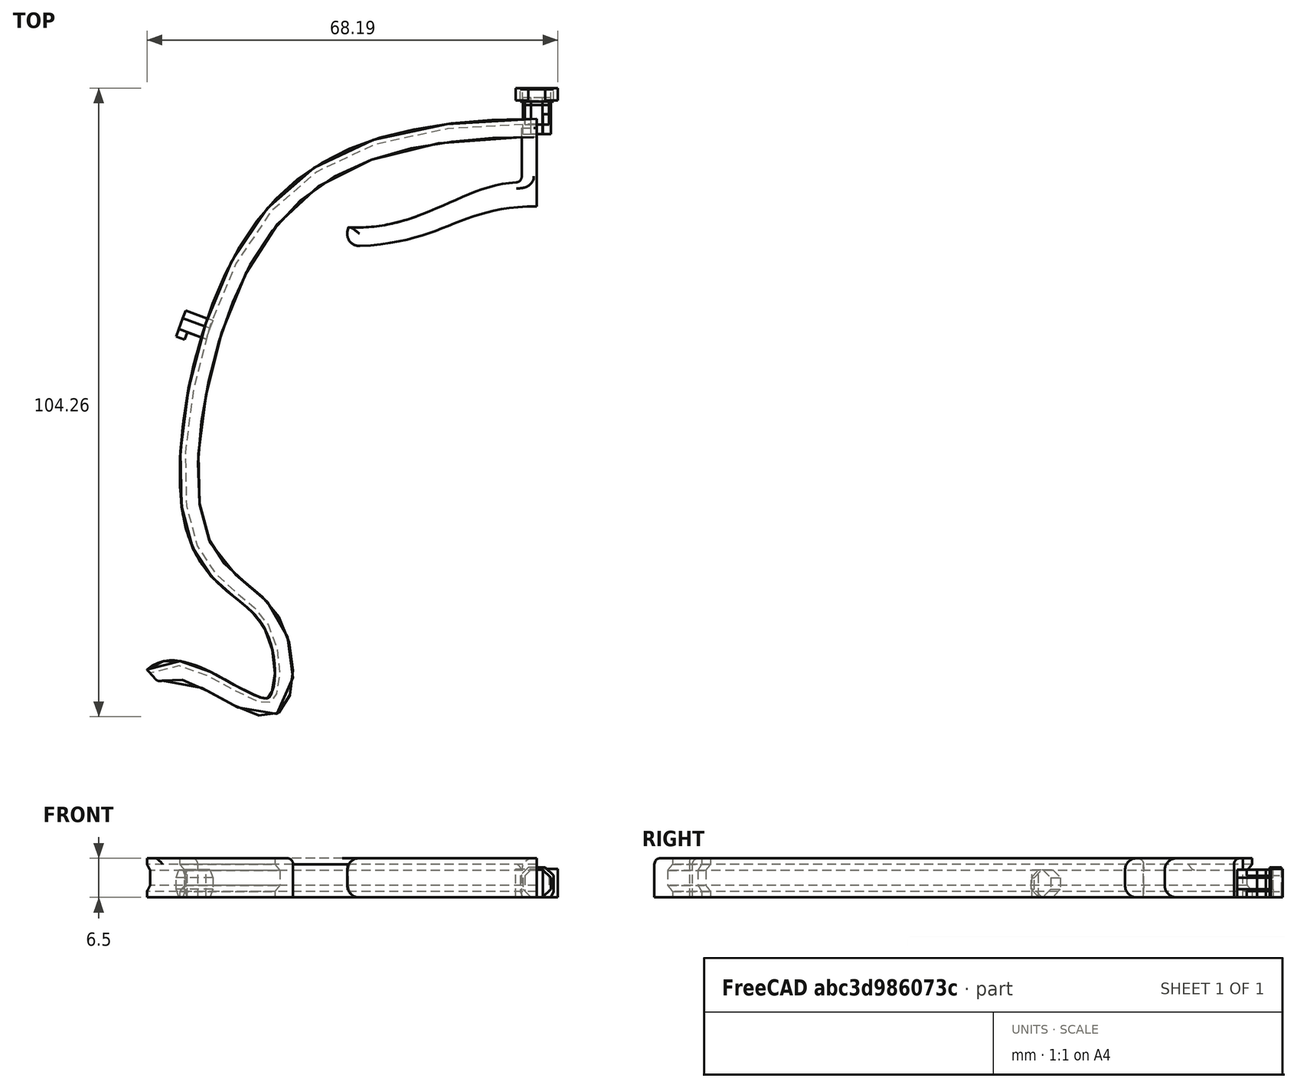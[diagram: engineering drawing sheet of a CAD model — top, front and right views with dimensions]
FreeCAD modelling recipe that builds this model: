
FCSTD DOCUMENT  (FreeCAD 0.18R16146 (Git))
Label: frame-001-02-a
License: All rights reserved
LicenseURL: http://ja.wikipedia.org/wiki/%E8%91%97%E4%BD%9C%E6%A8%A9%E8%A1%A8%E7%A4%BA
objects: Sketcher::SketchObject×5, Part::Extrusion×5, Part::Box×3, Part::Cut×2, Part::Fillet×2, Part::Compound×2, Mesh::Feature×1, Part::Sweep×1, Part::Mirroring×1, Part::MultiCommon×1
note: 22 computed .brp shape members not serialized (recipe doc carries the construction recipe); baked Part::Feature solids carry a one-line shape summary decoded from their .brp

FEATURE [Sketcher::SketchObject] Sketch  label="Sketch_FrameShape"
  sketch-geometry (15):
    g0-g7: Circle [constr] x8 (B-spline internal-alignment scaffolding for g8; pole/knot coordinates omitted)
    g8: BSplineCurve PolesCount=8 KnotsCount=6 Degree=3 IsPeriodic=0
    g9-g14: GeomPoint [constr] x6 (B-spline internal-alignment scaffolding for g8; pole/knot coordinates omitted)
  constraints (6):
    c: Radius(g0) = 6
    c: Equal(g0, g1-g6) x6
    c: InternalAlignment(g0-g7 -> g8) x8
    c: InternalAlignment(g9-g14 -> g8) x6
    c: Horizontal(g1,g8)
    c: Coincident(g-1,g8)
FEATURE [Sketcher::SketchObject] Sketch001
  Placement = pos=(0,0,0) rot=(0.57735,0.57735,0.57735;2.0944rad)
  sketch-geometry (8):
    g0: LineSegment StartX=-0.5 StartY=6.5 StartZ=0 EndX=2.5 EndY=6.5 EndZ=0
    g1: LineSegment StartX=2.5 StartY=6.5 StartZ=0 EndX=2.5 EndY=5.5 EndZ=0
    g2: LineSegment StartX=2.5 StartY=0 StartZ=0 EndX=-0.5 EndY=0 EndZ=0
    g3: LineSegment StartX=-0.5 StartY=0 StartZ=0 EndX=-0.5 EndY=6.5 EndZ=0
    g4: LineSegment StartX=2.5 StartY=5.5 StartZ=0 EndX=1.7 EndY=4.5 EndZ=0
    g5: LineSegment StartX=1.7 StartY=4.5 StartZ=0 EndX=1.7 EndY=2 EndZ=0
    g6: LineSegment StartX=1.7 StartY=2 StartZ=0 EndX=2.5 EndY=1 EndZ=0
    g7: LineSegment StartX=2.5 StartY=1 StartZ=0 EndX=2.5 EndY=0 EndZ=0
  constraints (24):
    c: Coincident(g0,g1)
    c: Coincident(g2,g3)
    c: Coincident(g3,g0)
    c: Horizontal(g0)
    c: Horizontal(g2)
    c: Vertical(g1)
    c: Vertical(g3)
    c: DistanceX(g0,g0) = 3
    c: DistanceY(g1,g0) = 1
    c: DistanceX(g-1,g2) = -0.5
    c: PointOnObject(g2,g-1)
    c: DistanceY(g2,g0) = 6.5
    c: Coincident(g1,g4)
    c: Coincident(g4,g5)
    c: Vertical(g5)
    c: Coincident(g5,g6)
    c: Coincident(g6,g7)
    c: Coincident(g7,g2)
    c: DistanceX(g2,g2) = 3
    c: Vertical(g7)
    c: DistanceY(g2,g6) = 1
    c: DistanceY(g6,g5) = 1
    c: DistanceY(g4,g1) = 1
    c: DistanceX(g2,g5) = 2.2
FEATURE [Mesh::Feature] cd43cbcc_75a4_11ea_893f_42010a00001e_UM3E_Visor_frame_EUROPE_ISO838_v3  label="cd43cbcc-75a4-11ea-893f-42010a00001e_UM3E_Visor_frame_EUROPE_ISO838_v3"
  Placement = pos=(0,-59,0) rot=(0,0,1;0rad)
FEATURE [Sketcher::SketchObject] Sketch002  label="OctPinSketch"
  Placement = pos=(0,0,0) rot=(1,0,0;1.5708rad)
  sketch-geometry (9):
    g0: LineSegment StartX=2.3097 StartY=1.35299 StartZ=0 EndX=2.3097 EndY=3.26641 EndZ=0
    g1: LineSegment StartX=2.3097 StartY=3.26641 StartZ=0 EndX=0.956709 EndY=4.6194 EndZ=0
    g2: LineSegment StartX=0.956709 StartY=4.6194 StartZ=0 EndX=-0.956709 EndY=4.6194 EndZ=0
    g3: LineSegment StartX=-0.956709 StartY=4.6194 StartZ=0 EndX=-2.3097 EndY=3.26641 EndZ=0
    g4: LineSegment StartX=-2.3097 StartY=3.26641 StartZ=0 EndX=-2.3097 EndY=1.35299 EndZ=0
    g5: LineSegment StartX=-2.3097 StartY=1.35299 StartZ=0 EndX=-0.956709 EndY=0 EndZ=0
    g6: LineSegment StartX=-0.956709 StartY=0 StartZ=0 EndX=0.956709 EndY=0 EndZ=0
    g7: LineSegment StartX=0.956709 StartY=0 StartZ=0 EndX=2.3097 EndY=1.35299 EndZ=0
    g8: Circle [constr] CenterX=0 CenterY=2.3097 CenterZ=0 NormalX=0 NormalY=0 NormalZ=1 AngleXU=0 Radius=2.5
  constraints (21):
    c: Coincident(g0,g1)
    c: Coincident(g1,g2)
    c: Coincident(g2,g3)
    c: Coincident(g3,g4)
    c: Coincident(g4,g5)
    c: Coincident(g5,g6)
    c: Coincident(g6,g7)
    c: Coincident(g7,g0)
    c: Equal(g0, g1-g7) x7
    c: PointOnObject(g0,g8)
    c: PointOnObject(g1,g8)
    c: PointOnObject(g2,g8)
    c: PointOnObject(g3,g8)
    c: PointOnObject(g4,g8)
    c: PointOnObject(g5,g8)
    c: PointOnObject(g6,g8)
    c: PointOnObject(g7,g8)
    c: Distance(g0,g8) = 2.5
    c: Horizontal(g6)
    c: PointOnObject(g8,g-2)
    c: PointOnObject(g6,g-1)
FEATURE [Part::Extrusion] Extrude002  label="OctPin"
  Base = -> Sketch002
  Dir = (0,-1,0)
  DirMode = 2
  FaceMakerClass = Part::FaceMakerBullseye
  LengthFwd = -6
  LengthRev = 0
  Solid = true
  Symmetric = false
FEATURE [Part::Extrusion] Extrude003  label="OctPinFront"
  Base = -> Sketch002
  Dir = (0,-1,2e-16)
  DirMode = 2
  FaceMakerClass = Part::FaceMakerBullseye
  LengthFwd = -3.8
  LengthRev = 0
  Placement = pos=(0,3,0) rot=(0,0,1;0rad)
  Solid = true
  Symmetric = false
FEATURE [Part::Extrusion] Extrude004  label="OctPin_WNotch_column"
  Base = -> Sketch002
  Dir = (0,-1,2e-16)
  DirMode = 2
  FaceMakerClass = Part::FaceMakerBullseye
  LengthFwd = -4.8
  LengthRev = 0
  Solid = true
  Symmetric = false
FEATURE [Part::Box] Box008  label="立方体008"
  AttacherType = Attacher::AttachEngine3D
  Height = 6
  Length = 2
  Placement = pos=(1,0,-0.5) rot=(0,0,1;0rad)
  Width = 3.3
FEATURE [Part::Cut] Cut  label="OctPin_WNotch"
  Base = -> Extrude004
  Tool = -> Box008
FEATURE [Part::Cut] Cut001  label="OctPin_WNotchR"
  Base = -> Extrude004
  Placement = pos=(54.56,-33.1,0) rot=(0,0,-1;1.22173rad)
  Tool = -> Box008
FEATURE [Sketcher::SketchObject] Sketch003
  sketch-geometry (18):
    g0: LineSegment StartX=0 StartY=1 StartZ=0 EndX=0 EndY=-12 EndZ=0
    g1: LineSegment StartX=2.5 StartY=-8 StartZ=0 EndX=2.5 EndY=1 EndZ=0
    g2: LineSegment StartX=2.5 StartY=1 StartZ=0 EndX=0 EndY=1 EndZ=0
    g3: LineSegment StartX=31.2873 StartY=-15.5 StartZ=0 EndX=31.8879 EndY=-18.6431 EndZ=0
    g4-g7: Circle [constr] x4 (B-spline internal-alignment scaffolding for g8; pole/knot coordinates omitted)
    g8: BSplineCurve PolesCount=4 KnotsCount=2 Degree=3 IsPeriodic=0
    g9: GeomPoint [constr] X=2.5 Y=-8 Z=0
    g10: GeomPoint [constr] X=31.2873 Y=-15.5 Z=0
    g11-g14: Circle [constr] x4 (B-spline internal-alignment scaffolding for g15; pole/knot coordinates omitted)
    g15: BSplineCurve PolesCount=4 KnotsCount=2 Degree=3 IsPeriodic=0
    g16: GeomPoint [constr] X=0 Y=-12 Z=0
    g17: GeomPoint [constr] X=31.8879 Y=-18.6431 Z=0
  constraints (32):
    c: PointOnObject(g0,g-2)
    c: Vertical(g0)
    c: Vertical(g1)
    c: Coincident(g1,g2)
    c: Coincident(g2,g0)
    c: DistanceX(g0,g1) = 2.5
    c: Horizontal(g2)
    c: DistanceY(g-1,g0) = 1
    c: DistanceY(g3,g1) = 7.5
    c: DistanceY(g0,g1) = 4
    c: DistanceY(g0,g-1) = 12
    c: Coincident(g8,g1)
    c: Radius(g4) = 2
    c: Equal(g4,g5)
    c: Equal(g4,g6)
    c: Equal(g4,g7)
    c: Coincident(g8,g3)
    c: InternalAlignment(g4-g7 -> g8) x4
    c: InternalAlignment(g9,g8)
    c: InternalAlignment(g10,g8)
    c: Coincident(g15,g0)
    c: Radius(g11) = 2
    c: Equal(g11,g12)
    c: Equal(g11,g13)
    c: Equal(g11,g14)
    c: Coincident(g15,g3)
    c: InternalAlignment(g11-g14 -> g15) x4
    c: InternalAlignment(g16,g15)
    c: InternalAlignment(g17,g15)
    c: Distance(g3,g3) = 3.2
    c: Horizontal(g0,g12)
    c: Horizontal(g5,g1)
FEATURE [Part::Extrusion] Extrude
  Base = -> Sketch003
  Dir = (0,0,1)
  DirMode = 2
  FaceMakerClass = Part::FaceMakerBullseye
  LengthFwd = 6.5
  LengthRev = 0
  Solid = true
  Symmetric = false
FEATURE [Part::Fillet] Fillet  label="AGOATE_R"
  Base = -> Extrude
  Edges = 8 edges: [Edge1 r=1,Edge4 r=2,Edge11 r=2,Edge12 r=2,Edge13 r=2,Edge15 r=2,Edge16 r=2,Edge18 r=1]
FEATURE [Part::Sweep] Sweep  label="Sweep_RightFrame"
  Frenet = false
  Sections = -> [Sketch001]
  Solid = true
  Spine = -> Sketch [Edge1]
  Transition = 1
FEATURE [Part::Fillet] Fillet001  label="Fillet_Sweep_RightFrame"
  Base = -> Sweep
  Edges = 2 edges r=1: [Edge1,Edge24]
FEATURE [Part::Compound] Compound  label="RightSide"
  Links = -> [Cut001,Fillet,Fillet001]
FEATURE [Part::Mirroring] Part__Mirroring001  label="LeftSide (Mirrored)"
  Base = (0,0,0)
  Normal = (1,0,0)
  Source = -> Compound
FEATURE [Part::Box] Box  label="立方体"
  AttacherType = Attacher::AttachEngine3D
  Height = 10
  Length = 4
  Placement = pos=(-2,2.8,0) rot=(0,0,1;0rad)
  Width = 4
FEATURE [Part::Box] Box010  label="立方体010"
  AttacherType = Attacher::AttachEngine3D
  Height = 4.7
  Length = 7
  Placement = pos=(-3.5,5.6,0) rot=(0,0,1;0rad)
  Width = 2
FEATURE [Part::MultiCommon] Common  label="前ダボ柱"
  Shapes = -> [Extrude003,Box]
FEATURE [Sketcher::SketchObject] Sketch004
  MapMode = 5
  Placement = pos=(0,6.8,0) rot=(0,0.707107,0.707107;3.14159rad)
  Support = -> [Common]
  sketch-geometry (8):
    g0: LineSegment StartX=-2.34451 StartY=0 StartZ=0 EndX=-2.75 EndY=1.00428 EndZ=0
    g1: LineSegment StartX=-2.75 StartY=1.00428 StartZ=0 EndX=-2.75 EndY=3.6504 EndZ=0
    g2: LineSegment StartX=-2.75 StartY=3.6504 StartZ=0 EndX=-1.4004 EndY=5 EndZ=0
    g3: LineSegment StartX=-1.4004 StartY=5 StartZ=0 EndX=1.4004 EndY=5 EndZ=0
    g4: LineSegment StartX=1.4004 StartY=5 StartZ=0 EndX=2.75 EndY=3.6504 EndZ=0
    g5: LineSegment StartX=2.75 StartY=3.6504 StartZ=0 EndX=2.75 EndY=1.00428 EndZ=0
    g6: LineSegment StartX=2.75 StartY=1.00428 StartZ=0 EndX=2.34451 EndY=0 EndZ=0
    g7: LineSegment StartX=2.34451 StartY=0 StartZ=0 EndX=-2.34451 EndY=0 EndZ=0
  constraints (17):
    c: Coincident(g0,g1)
    c: Coincident(g1,g2)
    c: Coincident(g2,g3)
    c: Coincident(g3,g4)
    c: Coincident(g4,g5)
    c: Coincident(g5,g6)
    c: Coincident(g6,g7)
    c: Coincident(g7,g0)
    c: Vertical(g1)
    c: Symmetric(g0,g6,g-2)
    c: Symmetric(g0,g5,g-2)
    c: Symmetric(g1,g4,g-2)
    c: Symmetric(g2,g3,g-2)
    c: PointOnObject(g6,g-1)
    c: DistanceY(g6,g3) = 5
    c: DistanceX(g0,g5) = 5.5
    c: Angle(g5,g4,g4) = 0.785398
FEATURE [Part::Extrusion] Extrude005  label="前ダボトメ"
  Base = -> Sketch004
  Dir = (0,1,-2e-16)
  DirMode = 2
  FaceMakerClass = Part::FaceMakerBullseye
  LengthFwd = 2
  LengthRev = 0
  Solid = true
  Symmetric = false
FEATURE [Part::Compound] Compound001  label="前ダボ"
  Links = -> [Common,Extrude005]
  Placement = pos=(0,-1.4,0) rot=(0,0,1;0rad)
